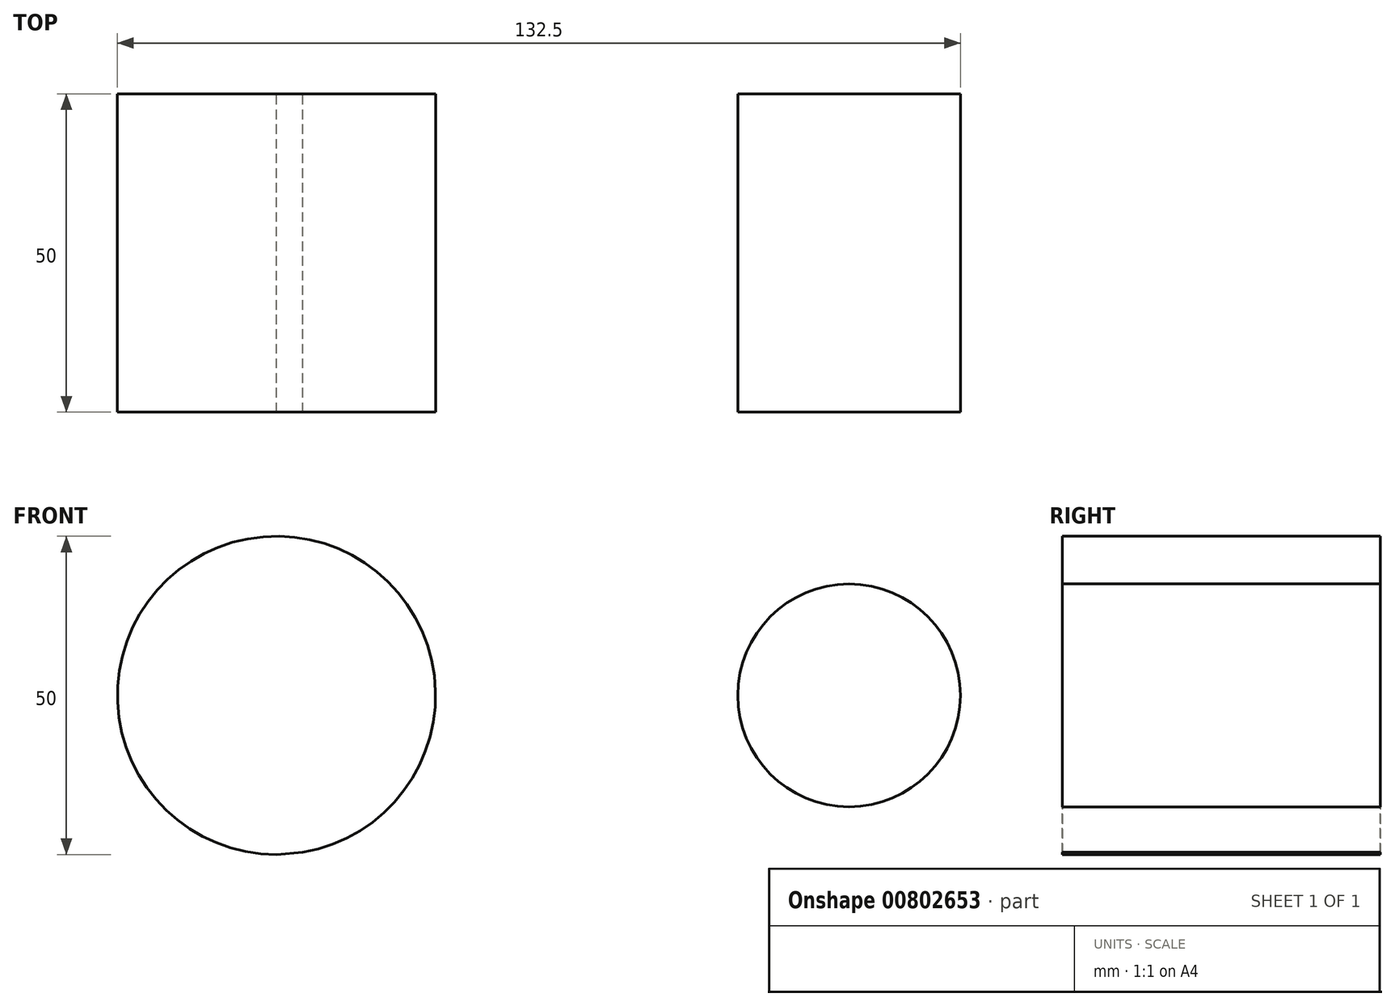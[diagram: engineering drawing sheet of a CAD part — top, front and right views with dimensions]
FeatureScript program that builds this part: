
annotation { "Feature Type Name" : "Feature", "Feature Type Description" : "" }
export const myFeature = defineFeature(function(context is Context, id is Id, definition is map)
    precondition{}
    {
        {
            var Q0;
            Q0=qCreatedBy(makeId("Front.planeOp"),FACE);
            var sketch = newSketch(context, id + "F0", { "sketchPlane" : qUnion([Q0])});
            skCircle(sketch, "E0", {"center": v(0, 0) * mm, "radius": 25 * mm});
            skCircle(sketch, "E1", {"center": v(90, 0) * mm, "radius": 17.5 * mm});
            skLineSegment(sketch, "E2", {"start": v(0, 25) * mm, "end": v(91.44, 17.44) * mm});
            skLineSegment(sketch, "E3", {"start": v(0, -25) * mm, "end": v(91.44, -17.44) * mm});
            skSolve(sketch);
        }
        {
            var Q0;
            {var subQ0=sQuery(id+"F0.wireOp",EDGE,"E2");var subQ1=sQuery(id+"F0.wireOp",EDGE,"E0");var subQ2=makeQuery(id+"F0.imprint","INTERSECT",VERTEX,{"disambiguationData":[OD(1.0)],"derivedFrom":[subQ1,subQ0]});Q0=makeQuery(id+"F0.imprint","IMPRINT",FACE,{"disambiguationData":[TD([[makeQuery(id+"F0.imprint","IMPRINT",EDGE,{"disambiguationData":[TD([[subQ2,1.0]])],"derivedFrom":subQ1}),-1.0]])]});}
            var Q1;
            {var subQ0=sQuery(id+"F0.wireOp",EDGE,"E2");var subQ1=sQuery(id+"F0.wireOp",EDGE,"E0");var subQ2=makeQuery(id+"F0.imprint","INTERSECT",VERTEX,{"disambiguationData":[OD(0.0)],"derivedFrom":[subQ1,subQ0]});Q1=makeQuery(id+"F0.imprint","IMPRINT",FACE,{"disambiguationData":[TD([[makeQuery(id+"F0.imprint","IMPRINT",EDGE,{"disambiguationData":[TD([[subQ2,1.0]])],"derivedFrom":subQ1}),1.0]])]});}
            var Q2;
            {var subQ0=sQuery(id+"F0.wireOp",EDGE,"E3");var subQ1=sQuery(id+"F0.wireOp",EDGE,"E0");var subQ2=makeQuery(id+"F0.imprint","INTERSECT",VERTEX,{"disambiguationData":[OD(0.0)],"derivedFrom":[subQ1,subQ0]});Q2=makeQuery(id+"F0.imprint","IMPRINT",FACE,{"disambiguationData":[TD([[makeQuery(id+"F0.imprint","IMPRINT",EDGE,{"disambiguationData":[TD([[subQ2,-1.0]])],"derivedFrom":subQ1}),1.0]])]});}
            var Q3;
            {var subQ0=sQuery(id+"F0.wireOp",EDGE,"E1");var subQ1=makeQuery(id+"F0.imprint","INTERSECT",VERTEX,{"derivedFrom":[subQ0,sQuery(id+"F0.wireOp",EDGE,"E2")]});Q3=makeQuery(id+"F0.imprint","IMPRINT",FACE,{"disambiguationData":[TD([[makeQuery(id+"F0.imprint","IMPRINT",EDGE,{"disambiguationData":[TD([[subQ1,-1.0]])],"derivedFrom":subQ0}),1.0]])]});}
            var Q4;
            {var subQ0=sQuery(id+"F0.wireOp",EDGE,"E2");var subQ1=sQuery(id+"F0.wireOp",EDGE,"E0");var subQ2=makeQuery(id+"F0.imprint","INTERSECT",VERTEX,{"disambiguationData":[OD(0.0)],"derivedFrom":[subQ1,subQ0]});Q4=makeQuery(id+"F0.imprint","IMPRINT",FACE,{"disambiguationData":[TD([[makeQuery(id+"F0.imprint","IMPRINT",EDGE,{"disambiguationData":[TD([[subQ2,-1.0]])],"derivedFrom":subQ1}),1.0]])]});}
            extrude(context, id + "F1", {"entities" : qUnion([Q0, Q1, Q2, Q3, Q4]), "depth" : 50 * mm, "offsetDistance" : 25.4 * mm});
        }
    });
